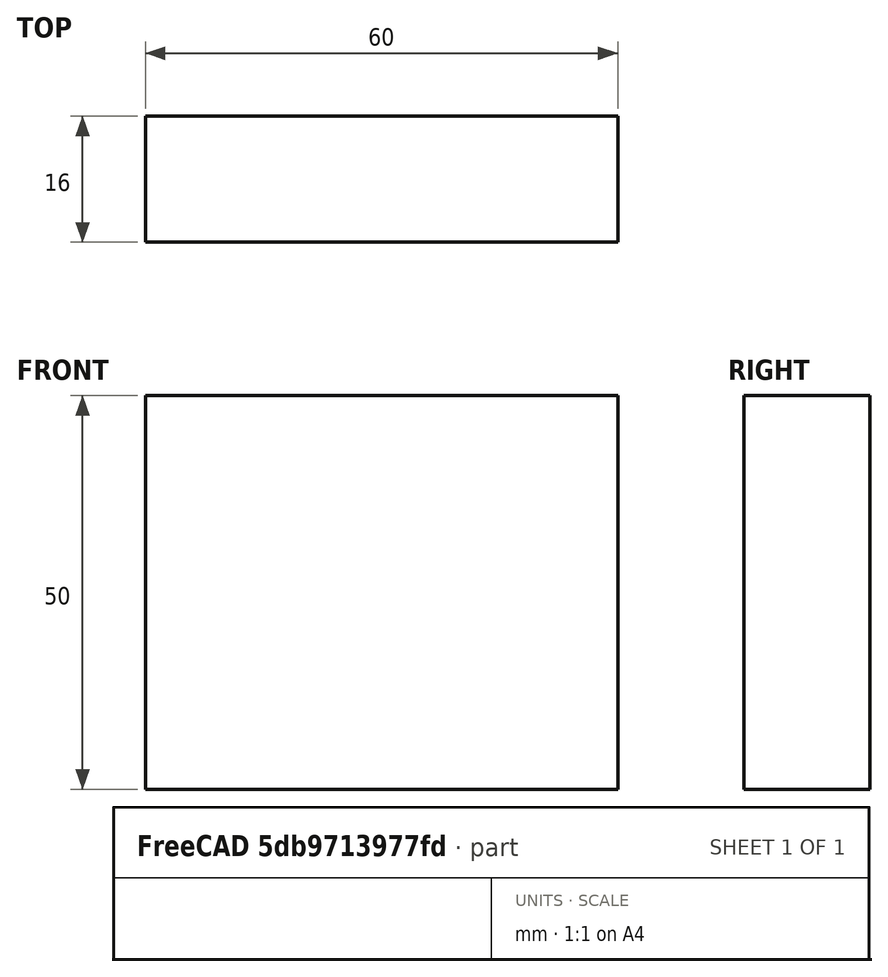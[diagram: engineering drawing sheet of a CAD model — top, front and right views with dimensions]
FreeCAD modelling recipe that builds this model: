
FCSTD DOCUMENT  (FreeCAD 0.15R4671 (Git))
Label: Flat Bar 60x16 EN10058 S235JR
License: All rights reserved
LicenseURL: http://en.wikipedia.org/wiki/All_rights_reserved
objects: Sketcher::SketchObject×1, Part::Extrusion×1
note: 2 computed .brp shape members not serialized (recipe doc carries the construction recipe); baked Part::Feature solids carry a one-line shape summary decoded from their .brp

FEATURE [Sketcher::SketchObject] Sketch
  sketch-geometry (4):
    g0: LineSegment StartX=-30 StartY=-8 StartZ=0 EndX=30 EndY=-8 EndZ=0
    g1: LineSegment StartX=30 StartY=-8 StartZ=0 EndX=30 EndY=8 EndZ=0
    g2: LineSegment StartX=30 StartY=8 StartZ=0 EndX=-30 EndY=8 EndZ=0
    g3: LineSegment StartX=-30 StartY=8 StartZ=0 EndX=-30 EndY=-8 EndZ=0
  constraints (12):
    c: Coincident(g0,g1)
    c: Coincident(g1,g2)
    c: Coincident(g2,g3)
    c: Coincident(g3,g0)
    c: Horizontal(g0)
    c: Horizontal(g2)
    c: Vertical(g1)
    c: Vertical(g3)
    c: Symmetric(g1,g2,g-2)
    c: Symmetric(g0,g1,g-1)
    c: DistanceY(g1) = 16
    c: DistanceX(g0) = 60
FEATURE [Part::Extrusion] Extrude  label="Flat Bar 60x16 EN10058 S235JR"
  Base = -> Sketch
  Dir = (0,0,50)
  Solid = true
